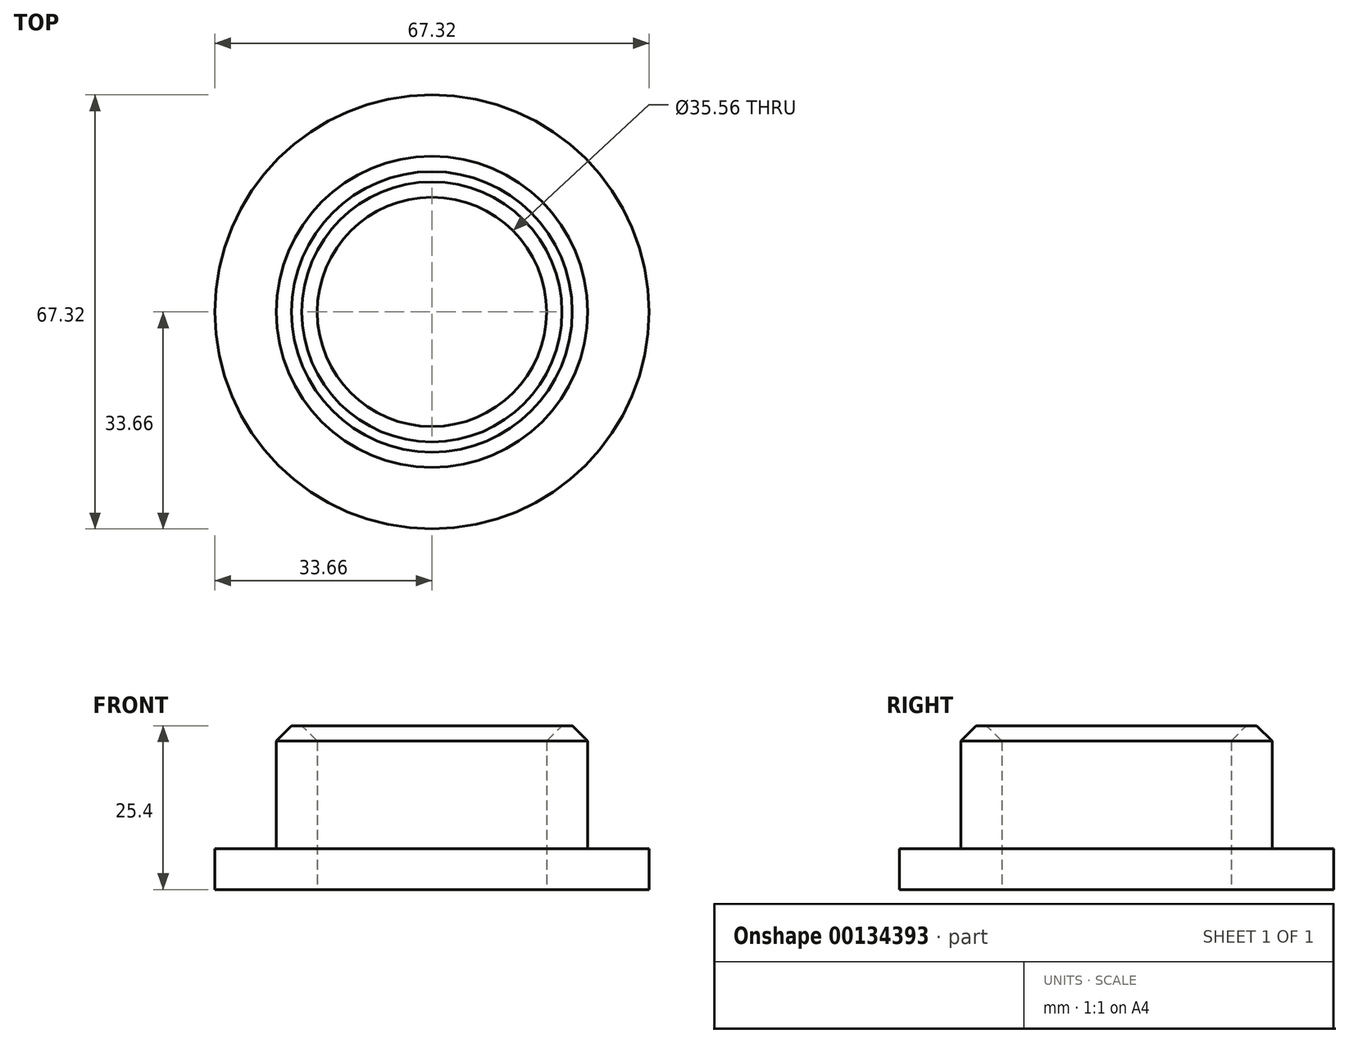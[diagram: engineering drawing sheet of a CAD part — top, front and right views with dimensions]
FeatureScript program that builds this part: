
annotation { "Feature Type Name" : "Feature", "Feature Type Description" : "" }
export const myFeature = defineFeature(function(context is Context, id is Id, definition is map)
    precondition{}
    {
        {
            var Q0;
            Q0=qCreatedBy(makeId("Top.planeOp"),FACE);
            var sketch = newSketch(context, id + "F0", { "sketchPlane" : qUnion([Q0])});
            skCircle(sketch, "E0", {"center": v(0, 0) * mm, "radius": 24.13 * mm});
            skCircle(sketch, "E1", {"center": v(0, 0) * mm, "radius": 17.78 * mm});
            skSolve(sketch);
        }
        {
            var Q0;
            Q0=makeQuery(id+"F0.imprint","IMPRINT",FACE,{"disambiguationData":[TD([[makeQuery(id+"F0.imprint","IMPRINT",EDGE,{"derivedFrom":sQuery(id+"F0.wireOp",EDGE,"E0")}),1.0]])]});
            extrude(context, id + "F1", {"entities" : qUnion([Q0]), "depth" : 25.4 * mm});
        }
        {
            var Q0;
            Q0=qCreatedBy(makeId("Top.planeOp"),FACE);
            var sketch = newSketch(context, id + "F2", { "sketchPlane" : qUnion([Q0])});
            skCircle(sketch, "E2", {"center": v(0, 0) * mm, "radius": 33.66 * mm});
            skCircle(sketch, "E3", {"center": v(0, 0) * mm, "radius": 24.13 * mm});
            skSolve(sketch);
        }
        {
            var Q0;
            Q0=makeQuery(id+"F2.imprint","IMPRINT",FACE,{"disambiguationData":[TD([[makeQuery(id+"F2.imprint","IMPRINT",EDGE,{"derivedFrom":sQuery(id+"F2.wireOp",EDGE,"E2")}),1.0]])]});
            extrude(context, id + "F3", {"entities" : qUnion([Q0]), "operationType" : NewBodyOperationType.ADD, "depth" : 6.35 * mm});
        }
        {
            var Q0;
            Q0=makeQuery(id+"F1.opExtrude","CAP_EDGE",EDGE,{"disambiguationData":[OSD([sQuery(id+"F0.wireOp",EDGE,"E0")])],"isStart":false});
            var Q1;
            Q1=makeQuery(id+"F1.opExtrude","CAP_EDGE",EDGE,{"disambiguationData":[OSD([sQuery(id+"F0.wireOp",EDGE,"E1")])],"isStart":false});
            chamfer(context, id + "F4", {"entities" : qUnion([Q0, Q1]), "width" : 2.38 * mm, "tangentPropagation" : true});
        }
    });
